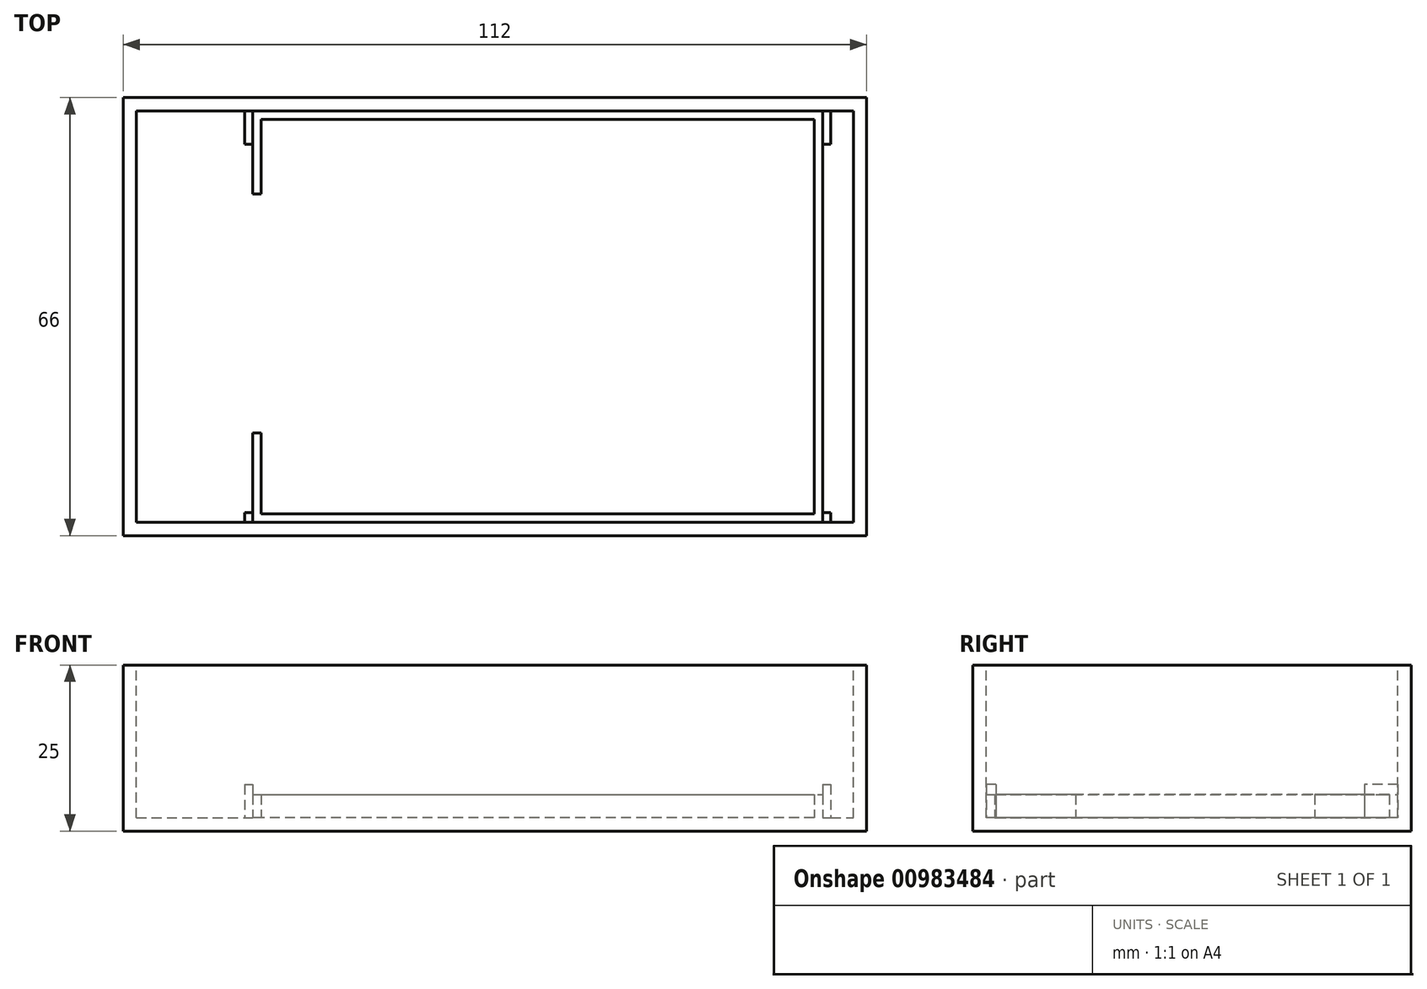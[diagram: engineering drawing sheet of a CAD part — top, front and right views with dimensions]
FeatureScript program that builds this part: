
annotation { "Feature Type Name" : "Feature", "Feature Type Description" : "" }
export const myFeature = defineFeature(function(context is Context, id is Id, definition is map)
    precondition{}
    {
        {
            var Q0;
            Q0=qCreatedBy(makeId("Top.planeOp"),FACE);
            var sketch = newSketch(context, id + "F0", { "sketchPlane" : qUnion([Q0])});
            skLineSegment(sketch, "E0.bottom", {"start": v(-49, 21.66) * mm, "end": v(63, 21.66) * mm});
            skLineSegment(sketch, "E0.top", {"start": v(-49, -44.34) * mm, "end": v(63, -44.34) * mm});
            skLineSegment(sketch, "E0.left", {"start": v(-49, 21.66) * mm, "end": v(-49, -44.34) * mm});
            skLineSegment(sketch, "E0.right", {"start": v(63, 21.66) * mm, "end": v(63, -44.34) * mm});
            skSolve(sketch);
        }
        {
            var Q0;
            Q0=makeQuery(id+"F0.imprint","IMPRINT",FACE,{"disambiguationData":[TD([[makeQuery(id+"F0.imprint","IMPRINT",EDGE,{"derivedFrom":sQuery(id+"F0.wireOp",EDGE,"E0.bottom")}),-1.0]])]});
            extrude(context, id + "F1", {"entities" : qUnion([Q0]), "depth" : 25 * mm, "offsetDistance" : 25 * mm});
        }
        {
            var Q0;
            Q0=makeQuery(id+"F1.opExtrude","CAP_FACE",FACE,{"disambiguationData":[OSD([sQuery(id+"F0.wireOp",EDGE,"E0.bottom"),sQuery(id+"F0.wireOp",EDGE,"E0.top"),sQuery(id+"F0.wireOp",EDGE,"E0.left"),sQuery(id+"F0.wireOp",EDGE,"E0.right")])],"isStart":false});
            var sketch = newSketch(context, id + "F2", { "sketchPlane" : qUnion([Q0])});
            skLineSegment(sketch, "E1.bottom", {"start": v(-47, 19.66) * mm, "end": v(61, 19.66) * mm});
            skLineSegment(sketch, "E1.top", {"start": v(-47, -42.34) * mm, "end": v(61, -42.34) * mm});
            skLineSegment(sketch, "E1.left", {"start": v(-47, 19.66) * mm, "end": v(-47, -42.34) * mm});
            skLineSegment(sketch, "E1.right", {"start": v(61, 19.66) * mm, "end": v(61, -42.34) * mm});
            skSolve(sketch);
        }
        {
            var Q0;
            Q0=makeQuery(id+"F2.imprint","IMPRINT",FACE,{"disambiguationData":[TD([[makeQuery(id+"F2.imprint","IMPRINT",EDGE,{"derivedFrom":sQuery(id+"F2.wireOp",EDGE,"E1.bottom")}),-1.0]])]});
            extrude(context, id + "F3", {"entities" : qUnion([Q0]), "operationType" : NewBodyOperationType.REMOVE, "oppositeDirection" : true, "depth" : 23 * mm, "offsetDistance" : 25 * mm});
        }
        {
            var Q0;
            Q0=makeQuery(id+"F3.boolean.opBoolean","COPY",FACE,{"derivedFrom":makeQuery(id+"F3.opExtrude","CAP_FACE",FACE,{"disambiguationData":[OSD([sQuery(id+"F2.wireOp",EDGE,"E1.bottom"),sQuery(id+"F2.wireOp",EDGE,"E1.top"),sQuery(id+"F2.wireOp",EDGE,"E1.left"),sQuery(id+"F2.wireOp",EDGE,"E1.right")])],"isStart":false})});
            var sketch = newSketch(context, id + "F4", { "sketchPlane" : qUnion([Q0])});
            skLineSegment(sketch, "E2", {"start": v(-28.2, 18.36) * mm, "end": v(55.1, 18.36) * mm});
            skLineSegment(sketch, "E3", {"start": v(55.1, 18.36) * mm, "end": v(55.1, -41.04) * mm});
            skLineSegment(sketch, "E4", {"start": v(55.1, -41.04) * mm, "end": v(-28.2, -41.04) * mm});
            skLineSegment(sketch, "E5", {"start": v(-28.2, -41.04) * mm, "end": v(-28.2, -28.84) * mm});
            skLineSegment(sketch, "E6", {"start": v(-28.2, -28.84) * mm, "end": v(-29.5, -28.84) * mm});
            skLineSegment(sketch, "E7", {"start": v(-29.5, -28.84) * mm, "end": v(-29.5, -42.34) * mm});
            skLineSegment(sketch, "E8", {"start": v(-29.5, -42.34) * mm, "end": v(56.4, -42.34) * mm});
            skLineSegment(sketch, "E9", {"start": v(56.4, -42.34) * mm, "end": v(56.4, 19.66) * mm});
            skLineSegment(sketch, "E10", {"start": v(56.4, 19.66) * mm, "end": v(-29.5, 19.66) * mm});
            skLineSegment(sketch, "E11", {"start": v(-29.5, 19.66) * mm, "end": v(-29.5, 7.16) * mm});
            skLineSegment(sketch, "E12", {"start": v(-29.5, 7.16) * mm, "end": v(-28.2, 7.16) * mm});
            skLineSegment(sketch, "E13", {"start": v(-28.2, 7.16) * mm, "end": v(-28.2, 18.36) * mm});
            skSolve(sketch);
        }
        {
            var Q0;
            Q0 = qSketchRegion(id + "F4", true);
            extrude(context, id + "F5", {"entities" : qUnion([Q0]), "operationType" : NewBodyOperationType.ADD, "depth" : 3.5 * mm, "offsetDistance" : 25 * mm});
        }
        {
            var Q0;
            {var subQ0=sQuery(id+"F2.wireOp",EDGE,"E1.bottom");var subQ1=sQuery(id+"F2.wireOp",EDGE,"E1.top");var subQ2=sQuery(id+"F2.wireOp",EDGE,"E1.left");Q0=makeQuery(id+"F5.boolean.opBoolean","SPLIT",FACE,{"disambiguationData":[TD([makeQuery(id+"F3.boolean.opBoolean","COPY",FACE,{"derivedFrom":makeQuery(id+"F3.opExtrude","SWEPT_FACE",FACE,{"disambiguationData":[OSD([subQ2])]})})])],"derivedFrom":makeQuery(id+"F3.boolean.opBoolean","COPY",FACE,{"derivedFrom":makeQuery(id+"F3.opExtrude","CAP_FACE",FACE,{"disambiguationData":[OSD([subQ0,subQ1,subQ2,sQuery(id+"F2.wireOp",EDGE,"E1.right")])],"isStart":false})})});}
            var sketch = newSketch(context, id + "F6", { "sketchPlane" : qUnion([Q0])});
            skLineSegment(sketch, "E14.bottom", {"start": v(56.4, 19.66) * mm, "end": v(57.6, 19.66) * mm});
            skLineSegment(sketch, "E14.top", {"start": v(56.4, 14.66) * mm, "end": v(57.6, 14.66) * mm});
            skLineSegment(sketch, "E14.left", {"start": v(56.4, 19.66) * mm, "end": v(56.4, 14.66) * mm});
            skLineSegment(sketch, "E14.right", {"start": v(57.6, 19.66) * mm, "end": v(57.6, 14.66) * mm});
            skLineSegment(sketch, "E15.bottom", {"start": v(-30.7, -40.84) * mm, "end": v(-29.5, -40.84) * mm});
            skLineSegment(sketch, "E15.top", {"start": v(-30.7, -42.34) * mm, "end": v(-29.5, -42.34) * mm});
            skLineSegment(sketch, "E15.left", {"start": v(-30.7, -40.84) * mm, "end": v(-30.7, -42.34) * mm});
            skLineSegment(sketch, "E15.right", {"start": v(-29.5, -40.84) * mm, "end": v(-29.5, -42.34) * mm});
            skLineSegment(sketch, "E16.bottom", {"start": v(56.4, -40.84) * mm, "end": v(57.6, -40.84) * mm});
            skLineSegment(sketch, "E16.top", {"start": v(56.4, -42.34) * mm, "end": v(57.6, -42.34) * mm});
            skLineSegment(sketch, "E16.left", {"start": v(56.4, -40.84) * mm, "end": v(56.4, -42.34) * mm});
            skLineSegment(sketch, "E16.right", {"start": v(57.6, -40.84) * mm, "end": v(57.6, -42.34) * mm});
            skLineSegment(sketch, "E17.bottom", {"start": v(-30.7, 19.66) * mm, "end": v(-29.5, 19.66) * mm});
            skLineSegment(sketch, "E17.top", {"start": v(-30.7, 14.66) * mm, "end": v(-29.5, 14.66) * mm});
            skLineSegment(sketch, "E17.left", {"start": v(-30.7, 19.66) * mm, "end": v(-30.7, 14.66) * mm});
            skLineSegment(sketch, "E17.right", {"start": v(-29.5, 19.66) * mm, "end": v(-29.5, 14.66) * mm});
            skSolve(sketch);
        }
        {
            var Q0;
            Q0 = qSketchRegion(id + "F6", true);
            extrude(context, id + "F7", {"entities" : qUnion([Q0]), "operationType" : NewBodyOperationType.ADD, "depth" : 5 * mm, "offsetDistance" : 25 * mm});
        }
    });
